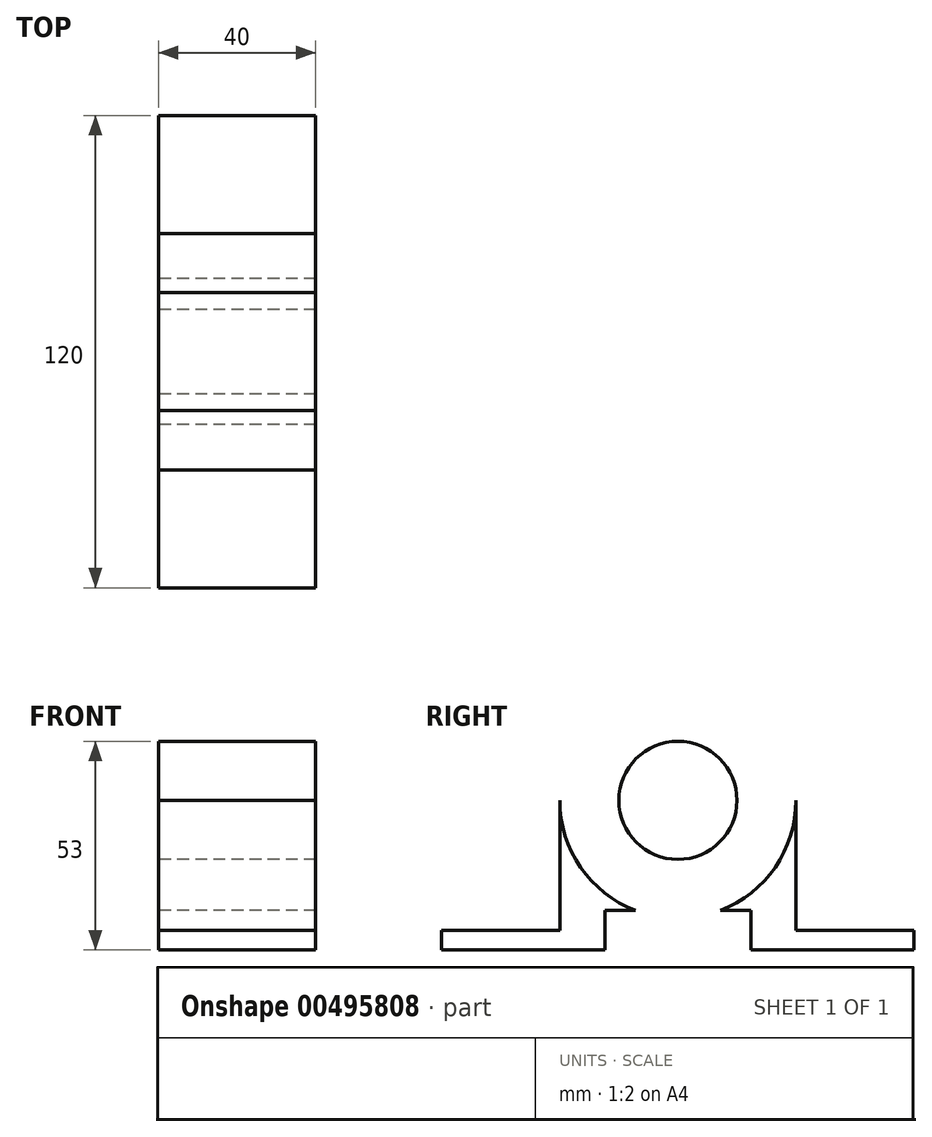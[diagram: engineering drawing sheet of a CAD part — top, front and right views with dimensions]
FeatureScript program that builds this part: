
annotation { "Feature Type Name" : "Feature", "Feature Type Description" : "" }
export const myFeature = defineFeature(function(context is Context, id is Id, definition is map)
    precondition{}
    {
        {
            var Q0;
            Q0=qCreatedBy(makeId("Right.planeOp"),FACE);
            var sketch = newSketch(context, id + "F0", { "sketchPlane" : qUnion([Q0])});
            skCircle(sketch, "E0", {"center": v(0, 0) * mm, "radius": 15 * mm});
            skCircle(sketch, "E1", {"center": v(0, 0) * mm, "radius": 30 * mm});
            skLineSegment(sketch, "E2.top", {"start": v(-30, -38) * mm, "end": v(21.25, -38) * mm});
            skLineSegment(sketch, "E2.left", {"start": v(-30, 0) * mm, "end": v(-30, -38) * mm});
            skLineSegment(sketch, "E2.right", {"start": v(21.25, 0) * mm, "end": v(21.25, -38) * mm});
            skLineSegment(sketch, "E3", {"start": v(-30, -38) * mm, "end": v(-27.07, -38) * mm});
            skLineSegment(sketch, "E4", {"start": v(-27.07, -38) * mm, "end": v(-27.07, -33) * mm});
            skLineSegment(sketch, "E5", {"start": v(-27.07, -33) * mm, "end": v(-60, -33) * mm});
            skLineSegment(sketch, "E6", {"start": v(-60, -33) * mm, "end": v(-60, -38) * mm});
            skLineSegment(sketch, "E7", {"start": v(-60, -38) * mm, "end": v(-30, -38) * mm});
            skLineSegment(sketch, "E8", {"start": v(-30, -38) * mm, "end": v(-18.53, -38) * mm});
            skLineSegment(sketch, "E9", {"start": v(-18.53, -38) * mm, "end": v(-18.53, -28) * mm});
            skLineSegment(sketch, "E10", {"start": v(-18.53, -28) * mm, "end": v(0, -28) * mm});
            skLineSegment(sketch, "E11", {"start": v(0, -28) * mm, "end": v(0, -38) * mm});
            skLineSegment(sketch, "E12.MirrorCS", {"start": v(30, -38) * mm, "end": v(27.07, -38) * mm});
            skLineSegment(sketch, "E13.MirrorCS", {"start": v(30, -38) * mm, "end": v(18.53, -38) * mm});
            skLineSegment(sketch, "E14.MirrorCS", {"start": v(60, -33) * mm, "end": v(60, -38) * mm});
            skLineSegment(sketch, "E15.MirrorCS", {"start": v(27.07, -38) * mm, "end": v(27.07, -33) * mm});
            skLineSegment(sketch, "E16.MirrorCS", {"start": v(60, -38) * mm, "end": v(30, -38) * mm});
            skLineSegment(sketch, "E17.MirrorCS", {"start": v(18.53, -38) * mm, "end": v(18.53, -28) * mm});
            skLineSegment(sketch, "E18.MirrorCS", {"start": v(27.07, -33) * mm, "end": v(60, -33) * mm});
            skLineSegment(sketch, "E19.MirrorCS", {"start": v(30, 0) * mm, "end": v(30, -38) * mm});
            skLineSegment(sketch, "E20.MirrorCS", {"start": v(-21.25, 0) * mm, "end": v(-21.25, -38) * mm});
            skLineSegment(sketch, "E21.MirrorCS", {"start": v(18.53, -28) * mm, "end": v(0, -28) * mm});
            skLineSegment(sketch, "E22.MirrorCS", {"start": v(30, -38) * mm, "end": v(-21.25, -38) * mm});
            skSolve(sketch);
        }
        {
            var Q0;
            {var subQ4=sQuery(id+"F0.wireOp",EDGE,"E6");Q0=makeQuery(id+"F0.imprint","IMPRINT",FACE,{"disambiguationData":[TD([[makeQuery(id+"F0.imprint","IMPRINT",EDGE,{"derivedFrom":subQ4}),1.0]])]});}
            var Q1;
            {var subQ0=sQuery(id+"F0.wireOp",EDGE,"E14.MirrorCS");Q1=makeQuery(id+"F0.imprint","IMPRINT",FACE,{"disambiguationData":[TD([[makeQuery(id+"F0.imprint","IMPRINT",EDGE,{"derivedFrom":subQ0}),-1.0]])]});}
            var Q2;
            {var subQ5=sQuery(id+"F0.wireOp",EDGE,"E4");Q2=makeQuery(id+"F0.imprint","IMPRINT",FACE,{"disambiguationData":[TD([[makeQuery(id+"F0.imprint","IMPRINT",EDGE,{"derivedFrom":subQ5}),1.0]])]});}
            var Q3;
            {var subQ0=sQuery(id+"F0.wireOp",EDGE,"E15.MirrorCS");Q3=makeQuery(id+"F0.imprint","IMPRINT",FACE,{"disambiguationData":[TD([[makeQuery(id+"F0.imprint","IMPRINT",EDGE,{"derivedFrom":subQ0}),-1.0]])]});}
            var Q4;
            {var subQ1=sQuery(id+"F0.wireOp",EDGE,"E4");Q4=makeQuery(id+"F0.imprint","IMPRINT",FACE,{"disambiguationData":[TD([[makeQuery(id+"F0.imprint","IMPRINT",EDGE,{"derivedFrom":subQ1}),-1.0]])]});}
            var Q5;
            {var subQ5=sQuery(id+"F0.wireOp",EDGE,"E15.MirrorCS");Q5=makeQuery(id+"F0.imprint","IMPRINT",FACE,{"disambiguationData":[TD([[makeQuery(id+"F0.imprint","IMPRINT",EDGE,{"derivedFrom":subQ5}),1.0]])]});}
            var Q6;
            {var subQ3=sQuery(id+"F0.wireOp",EDGE,"E17.MirrorCS");Q6=makeQuery(id+"F0.imprint","IMPRINT",FACE,{"disambiguationData":[TD([[makeQuery(id+"F0.imprint","IMPRINT",EDGE,{"derivedFrom":subQ3}),-1.0]])]});}
            var Q7;
            {var subQ5=sQuery(id+"F0.wireOp",EDGE,"E9");Q7=makeQuery(id+"F0.imprint","IMPRINT",FACE,{"disambiguationData":[TD([[makeQuery(id+"F0.imprint","IMPRINT",EDGE,{"derivedFrom":subQ5}),1.0]])]});}
            var Q8;
            Q8=makeQuery(id+"F0.imprint","IMPRINT",FACE,{"disambiguationData":[TD([[makeQuery(id+"F0.imprint","IMPRINT",EDGE,{"derivedFrom":sQuery(id+"F0.wireOp",EDGE,"E0")}),1.0]])]});
            extrude(context, id + "F1", {"entities" : qUnion([Q0, Q1, Q2, Q3, Q4, Q5, Q6, Q7, Q8]), "depth" : 40 * mm});
        }
    });
